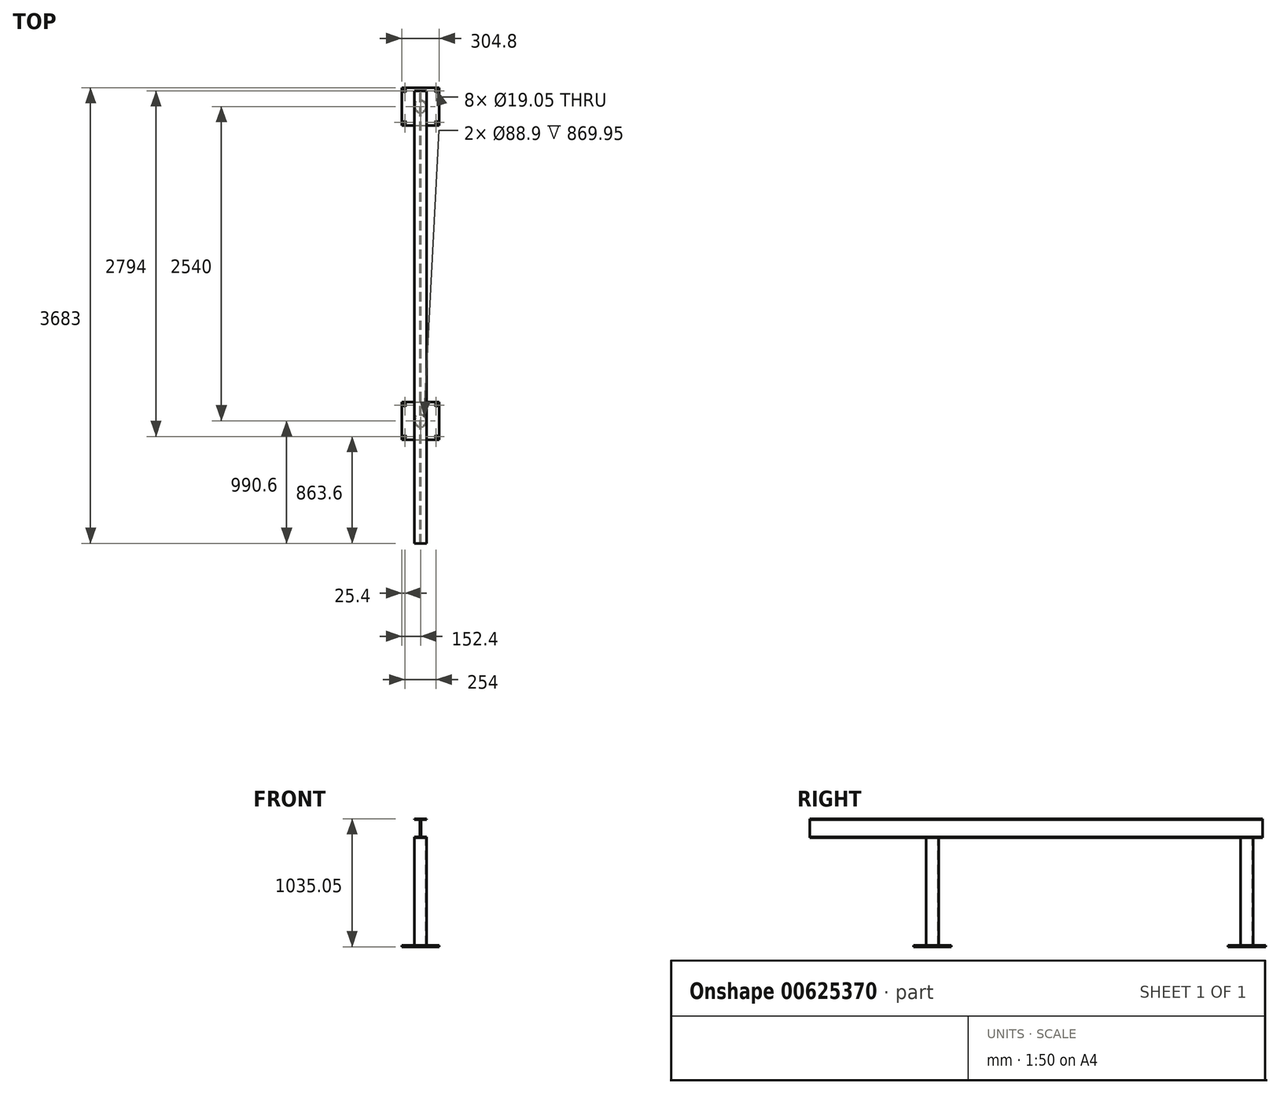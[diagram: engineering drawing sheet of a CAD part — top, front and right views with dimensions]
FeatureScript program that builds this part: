
annotation { "Feature Type Name" : "Feature", "Feature Type Description" : "" }
export const myFeature = defineFeature(function(context is Context, id is Id, definition is map)
    precondition{}
    {
        {
            var Q0;
            Q0=qCreatedBy(makeId("Front.planeOp"),FACE);
            var sketch = newSketch(context, id + "F0", { "sketchPlane" : qUnion([Q0])});
            skLineSegment(sketch, "E0.bottom", {"start": v(-3.17, 76.2) * mm, "end": v(3.18, 76.2) * mm});
            skLineSegment(sketch, "E0.top", {"start": v(-3.18, -76.2) * mm, "end": v(3.17, -76.2) * mm});
            skLineSegment(sketch, "E0.left", {"start": v(-3.17, 69.85) * mm, "end": v(-3.18, -69.85) * mm});
            skLineSegment(sketch, "E0.right", {"start": v(3.18, 69.85) * mm, "end": v(3.17, -69.85) * mm});
            skPoint(sketch, "E0.middle", {"position": v(0, 73.02) * mm});
            skLineSegment(sketch, "E1.bottom", {"start": v(-50.8, 76.2) * mm, "end": v(50.8, 76.2) * mm});
            skLineSegment(sketch, "E1.top", {"start": v(-50.8, 69.85) * mm, "end": v(-3.17, 69.85) * mm});
            skLineSegment(sketch, "E1.left", {"start": v(-50.8, 76.2) * mm, "end": v(-50.8, 69.85) * mm});
            skLineSegment(sketch, "E1.right", {"start": v(50.8, 76.2) * mm, "end": v(50.8, 69.85) * mm});
            skLineSegment(sketch, "E2.bottom", {"start": v(50.8, -69.85) * mm, "end": v(3.17, -69.85) * mm});
            skLineSegment(sketch, "E2.top", {"start": v(50.8, -76.2) * mm, "end": v(3.17, -76.2) * mm});
            skLineSegment(sketch, "E2.left", {"start": v(50.8, -69.85) * mm, "end": v(50.8, -76.2) * mm});
            skLineSegment(sketch, "E2.right", {"start": v(-50.8, -69.85) * mm, "end": v(-50.8, -76.2) * mm});
            skPoint(sketch, "E2.middle", {"position": v(0, -73.03) * mm});
            skLineSegment(sketch, "E3.trimOffspring", {"start": v(-3.18, -76.2) * mm, "end": v(-50.8, -76.2) * mm});
            skLineSegment(sketch, "E4.trimOffspring", {"start": v(-3.18, -69.85) * mm, "end": v(-50.8, -69.85) * mm});
            skLineSegment(sketch, "E5.trimOffspring", {"start": v(3.18, 69.85) * mm, "end": v(50.8, 69.85) * mm});
            skSolve(sketch);
        }
        {
            var Q0;
            Q0=makeQuery(id+"F0.imprint","IMPRINT",FACE,{"disambiguationData":[TD([[makeQuery(id+"F0.imprint","IMPRINT",EDGE,{"derivedFrom":sQuery(id+"F0.wireOp",EDGE,"E0.top")}),1.0]])]});
            extrude(context, id + "F1", {"entities" : qUnion([Q0]), "depth" : 3657.6 * mm, "offsetDistance" : 25.4 * mm});
        }
        {
            var Q0;
            Q0=qCreatedBy(makeId("Top.planeOp"),FACE);
            var sketch = newSketch(context, id + "F2", { "sketchPlane" : qUnion([Q0])});
            skCircle(sketch, "E6", {"center": v(0, 76.2) * mm, "radius": 50.8 * mm});
            skCircle(sketch, "E7", {"center": v(0, 76.2) * mm, "radius": 44.45 * mm});
            skSolve(sketch);
        }
        {
            var Q0;
            Q0=makeQuery(id+"F2.imprint","IMPRINT",FACE,{"disambiguationData":[TD([[makeQuery(id+"F2.imprint","IMPRINT",EDGE,{"derivedFrom":sQuery(id+"F2.wireOp",EDGE,"E6")}),1.0]])]});
            extrude(context, id + "F3", {"entities" : qUnion([Q0]), "operationType" : NewBodyOperationType.ADD, "oppositeDirection" : true, "depth" : 869.95 * mm, "offsetDistance" : 25.4 * mm});
        }
        {
            var Q0;
            Q0=makeQuery(id+"F3.opExtrude","SWEPT_BODY",BODY,{"disambiguationData":[OSD([sQuery(id+"F2.wireOp",EDGE,"E6"),sQuery(id+"F2.wireOp",EDGE,"E7")])]});
            var Q1;
            Q1=qCreatedBy(makeId("Top.planeOp"),FACE);
            transform(context, id + "F4", {"entities" : qUnion([Q0]), "transformType" : TransformType.TRANSLATION_DISTANCE, "transformDirection" : qUnion([Q1]), "distance" : 76.2 * mm, "oppositeDirection" : true, "makeCopy" : false});
        }
        {
            var Q0;
            Q0=makeQuery(id+"F3.opExtrude","SWEPT_BODY",BODY,{"disambiguationData":[OSD([sQuery(id+"F2.wireOp",EDGE,"E6"),sQuery(id+"F2.wireOp",EDGE,"E7")])]});
            var Q1;
            Q1=qCreatedBy(makeId("Front.planeOp"),FACE);
            transform(context, id + "F5", {"entities" : qUnion([Q0]), "transformType" : TransformType.TRANSLATION_DISTANCE, "transformDirection" : qUnion([Q1]), "distance" : 203.2 * mm, "makeCopy" : false});
        }
        {
            var Q0;
            Q0=makeQuery(id+"F3.opExtrude","SWEPT_BODY",BODY,{"disambiguationData":[OSD([sQuery(id+"F2.wireOp",EDGE,"E6"),sQuery(id+"F2.wireOp",EDGE,"E7")])]});
            var Q1;
            Q1=qCreatedBy(makeId("Front.planeOp"),FACE);
            transform(context, id + "F6", {"entities" : qUnion([Q0]), "transformType" : TransformType.TRANSLATION_DISTANCE, "transformDirection" : qUnion([Q1]), "distance" : 2540 * mm, "makeCopy" : true});
        }
        {
            var Q0;
            Q0=makeQuery(id+"F6.opPattern","COPY",FACE,{"derivedFrom":makeQuery(id+"F3.opExtrude","CAP_FACE",FACE,{"disambiguationData":[OSD([sQuery(id+"F2.wireOp",EDGE,"E6"),sQuery(id+"F2.wireOp",EDGE,"E7")])],"isStart":false}),"instanceName":"1"});
            var sketch = newSketch(context, id + "F7", { "sketchPlane" : qUnion([Q0])});
            skLineSegment(sketch, "E8.bottom", {"start": v(-152.4, 2514.6) * mm, "end": v(152.4, 2514.6) * mm});
            skLineSegment(sketch, "E8.top", {"start": v(-152.4, 2819.4) * mm, "end": v(152.4, 2819.4) * mm});
            skLineSegment(sketch, "E8.left", {"start": v(-152.4, 2514.6) * mm, "end": v(-152.4, 2819.4) * mm});
            skLineSegment(sketch, "E8.right", {"start": v(152.4, 2514.6) * mm, "end": v(152.4, 2819.4) * mm});
            skPoint(sketch, "E8.middle", {"position": v(0, 2667) * mm});
            skCircle(sketch, "E9", {"center": v(-127, 2540) * mm, "radius": 9.53 * mm});
            skCircle(sketch, "E10", {"center": v(127, 2540) * mm, "radius": 9.53 * mm});
            skCircle(sketch, "E11", {"center": v(-127, 2794) * mm, "radius": 9.53 * mm});
            skCircle(sketch, "E12", {"center": v(127, 2794) * mm, "radius": 9.53 * mm});
            skSolve(sketch);
        }
        {
            var Q0;
            Q0=makeQuery(id+"F7.imprint","IMPRINT",FACE,{"disambiguationData":[TD([[makeQuery(id+"F7.imprint","IMPRINT",EDGE,{"derivedFrom":sQuery(id+"F7.wireOp",EDGE,"E8.bottom")}),1.0]])]});
            var Q1;
            Q1=makeQuery(id+"F7.imprint","IMPRINT",FACE,{"disambiguationData":[TD([[makeQuery(id+"F7.imprint","IMPRINT",EDGE,{"derivedFrom":makeQuery(id+"F6.opPattern","COPY",EDGE,{"derivedFrom":makeQuery(id+"F3.opExtrude","CAP_EDGE",EDGE,{"disambiguationData":[OSD([sQuery(id+"F2.wireOp",EDGE,"E6")])],"isStart":false}),"instanceName":"1"})}),-1.0]])]});
            var Q2;
            Q2=makeQuery(id+"F7.imprint","IMPRINT",FACE,{"disambiguationData":[TD([[makeQuery(id+"F7.imprint","IMPRINT",EDGE,{"derivedFrom":makeQuery(id+"F6.opPattern","COPY",EDGE,{"derivedFrom":makeQuery(id+"F3.opExtrude","CAP_EDGE",EDGE,{"disambiguationData":[OSD([sQuery(id+"F2.wireOp",EDGE,"E7")])],"isStart":false}),"instanceName":"1"})}),-1.0]])]});
            extrude(context, id + "F8", {"entities" : qUnion([Q0, Q1, Q2]), "depth" : 12.7 * mm, "offsetDistance" : 25.4 * mm});
        }
        {
            var Q0;
            Q0=makeQuery(id+"F8.opExtrude","SWEPT_BODY",BODY,{"disambiguationData":[OSD([sQuery(id+"F7.wireOp",EDGE,"E8.bottom"),sQuery(id+"F7.wireOp",EDGE,"E8.top"),sQuery(id+"F7.wireOp",EDGE,"E8.left"),sQuery(id+"F7.wireOp",EDGE,"E8.right"),sQuery(id+"F7.wireOp",EDGE,"E9"),sQuery(id+"F7.wireOp",EDGE,"E10"),sQuery(id+"F7.wireOp",EDGE,"E11"),sQuery(id+"F7.wireOp",EDGE,"E12")])]});
            var Q1;
            Q1=qCreatedBy(makeId("Front.planeOp"),FACE);
            transform(context, id + "F9", {"entities" : qUnion([Q0]), "transformType" : TransformType.TRANSLATION_DISTANCE, "transformDirection" : qUnion([Q1]), "distance" : 2540 * mm, "oppositeDirection" : true, "makeCopy" : true});
        }
    });
